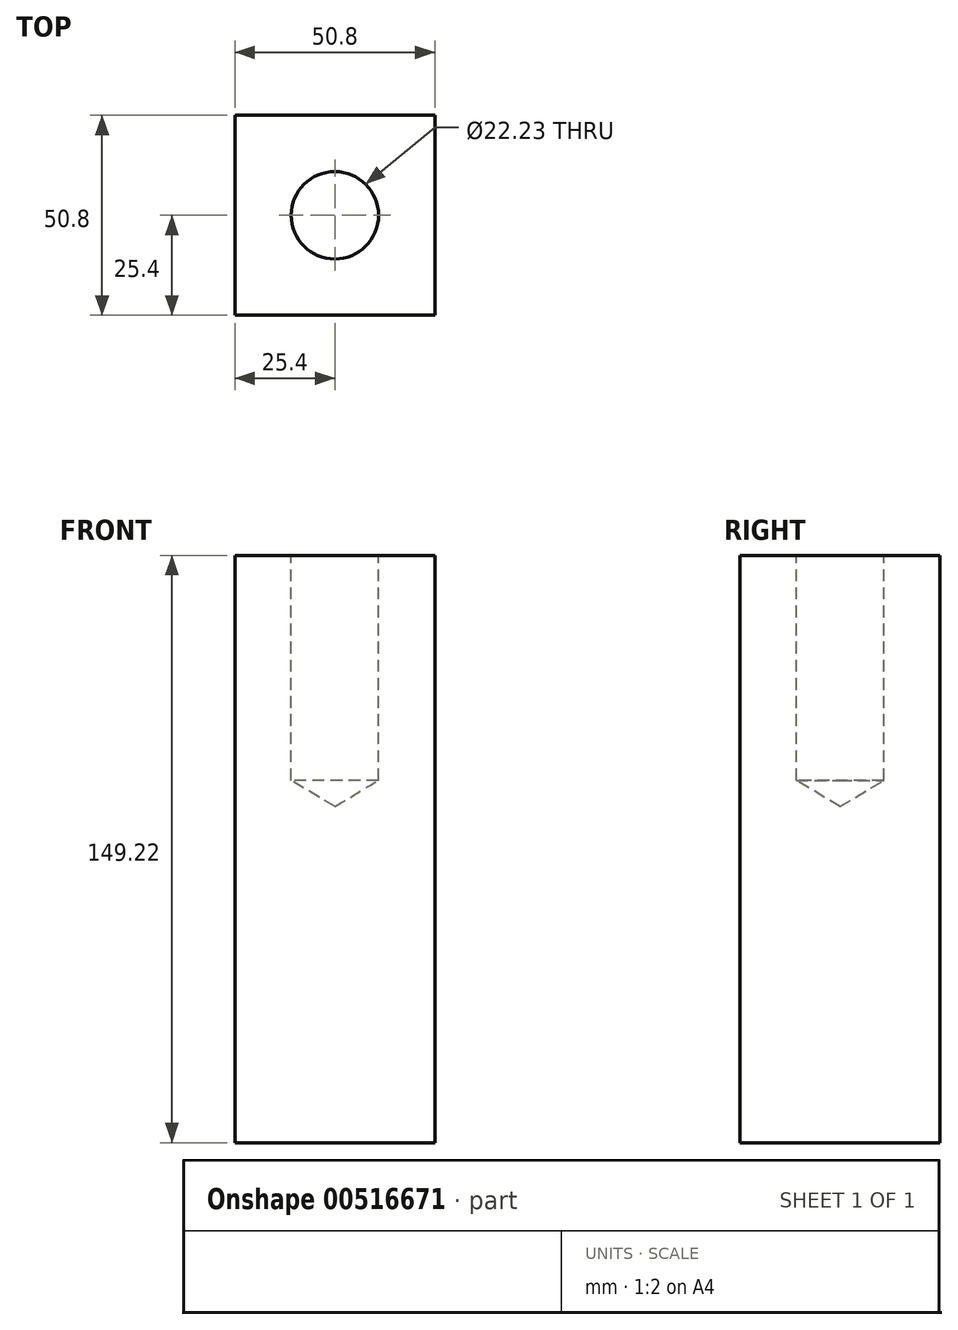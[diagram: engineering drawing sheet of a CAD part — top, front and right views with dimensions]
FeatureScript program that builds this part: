
annotation { "Feature Type Name" : "Feature", "Feature Type Description" : "" }
export const myFeature = defineFeature(function(context is Context, id is Id, definition is map)
    precondition{}
    {
        {
            var Q0;
            Q0=qCreatedBy(makeId("Top.planeOp"),FACE);
            var sketch = newSketch(context, id + "F0", { "sketchPlane" : qUnion([Q0])});
            skLineSegment(sketch, "E0.bottom", {"start": v(25.4, 25.4) * mm, "end": v(-25.4, 25.4) * mm});
            skLineSegment(sketch, "E0.top", {"start": v(25.4, -25.4) * mm, "end": v(-25.4, -25.4) * mm});
            skLineSegment(sketch, "E0.left", {"start": v(25.4, 25.4) * mm, "end": v(25.4, -25.4) * mm});
            skLineSegment(sketch, "E0.right", {"start": v(-25.4, 25.4) * mm, "end": v(-25.4, -25.4) * mm});
            skPoint(sketch, "E0.middle", {"position": v(0, 0) * mm});
            skSolve(sketch);
        }
        {
            var Q0;
            Q0=makeQuery(id+"F0.imprint","IMPRINT",FACE,{"disambiguationData":[TD([[makeQuery(id+"F0.imprint","IMPRINT",EDGE,{"derivedFrom":sQuery(id+"F0.wireOp",EDGE,"E0.bottom")}),1.0]])]});
            extrude(context, id + "F1", {"entities" : qUnion([Q0]), "endBound" : BoundingType.SYMMETRIC, "depth" : 149.22 * mm, "offsetDistance" : 25.4 * mm});
        }
        {
            var Q0;
            Q0=makeQuery(id+"F1.opExtrude","CAP_FACE",FACE,{"disambiguationData":[OSD([sQuery(id+"F0.wireOp",EDGE,"E0.bottom"),sQuery(id+"F0.wireOp",EDGE,"E0.top"),sQuery(id+"F0.wireOp",EDGE,"E0.left"),sQuery(id+"F0.wireOp",EDGE,"E0.right")])],"isStart":false});
            var sketch = newSketch(context, id + "F2", { "sketchPlane" : qUnion([Q0])});
            skPoint(sketch, "E1", {"position": v(0, 0) * mm});
            skSolve(sketch);
        }
        {
            var Q0;
            Q0=sQuery(id+"F2.wireOp",VERTEX,"E1");
            var Q1;
            Q1=makeQuery(id+"F1.opExtrude","SWEPT_BODY",BODY,{"disambiguationData":[OSD([sQuery(id+"F0.wireOp",EDGE,"E0.bottom"),sQuery(id+"F0.wireOp",EDGE,"E0.top"),sQuery(id+"F0.wireOp",EDGE,"E0.left"),sQuery(id+"F0.wireOp",EDGE,"E0.right")])]});
            hole(context, id + "F3", {"style" : HoleStyle.SIMPLE, "endStyle" : HoleEndStyle.BLIND, "standardTappedOrClearance" : lookupTablePath({ "standard" : "ANSI", "engagement" : "75%", "pitch" : "8 tpi", "size" : "1", "type" : "Tapped" }), "standardBlindInLast" : lookupTablePath({ "standard" : "ANSI", "engagement" : "75%", "pitch" : "8 tpi", "size" : "1", "type" : "Tapped" }), "holeDiameter" : 22.22 * mm, "showTappedDepth" : true, "holeDepth" : 57.15 * mm, "isTappedThrough" : true, "tappedDepth" : 47.62 * mm, "tapClearance" : 3, "startFromSketch" : true, "locations" : qUnion([Q0]), "scope" : qUnion([Q1]), "majorDiameter" : 25.4 * mm});
        }
    });
